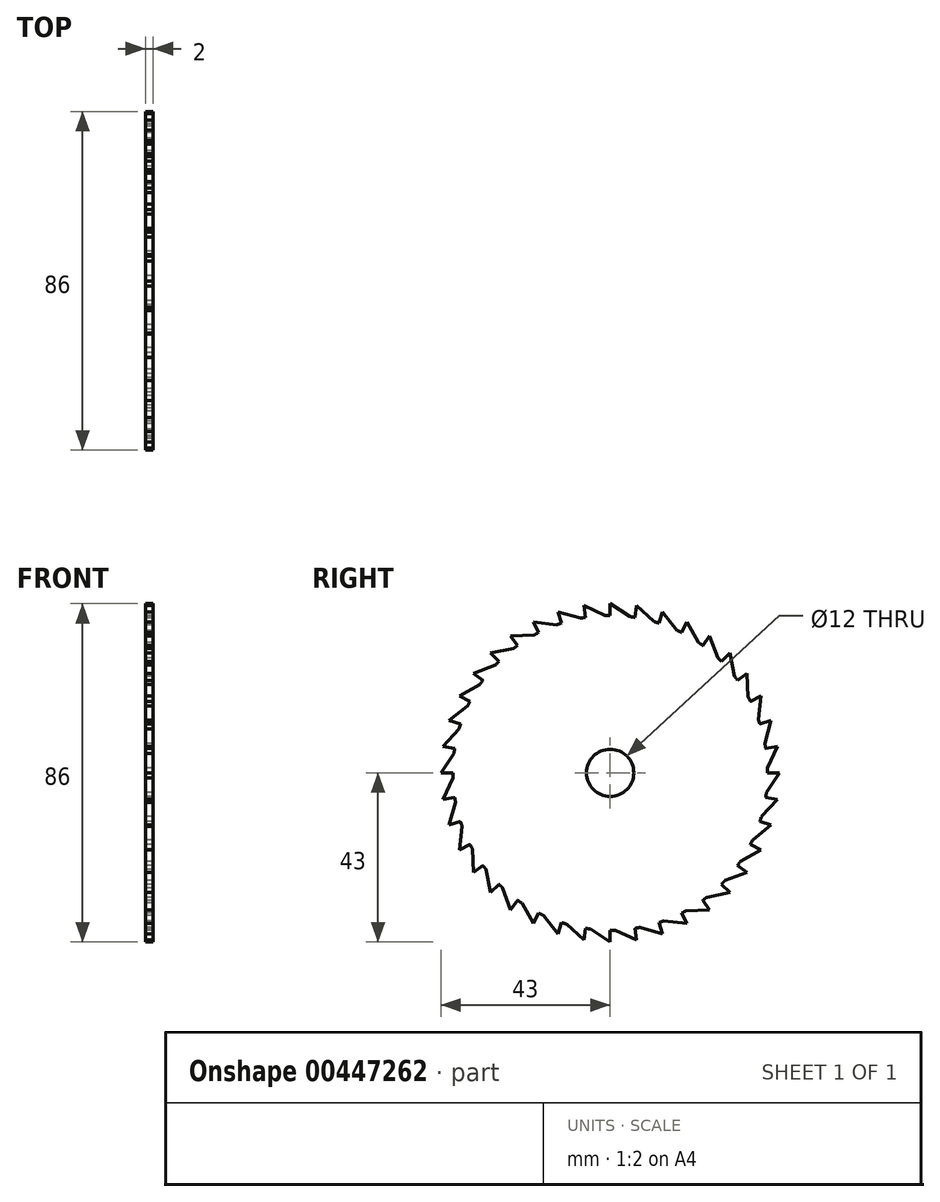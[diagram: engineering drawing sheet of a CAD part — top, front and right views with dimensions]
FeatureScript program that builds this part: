
annotation { "Feature Type Name" : "Feature", "Feature Type Description" : "" }
export const myFeature = defineFeature(function(context is Context, id is Id, definition is map)
    precondition{}
    {
        {
            var Q0;
            Q0=qCreatedBy(makeId("Right.planeOp"),FACE);
            var sketch = newSketch(context, id + "F0", { "sketchPlane" : qUnion([Q0])});
            skCircle(sketch, "E0", {"center": v(0, 0) * mm, "radius": 40 * mm});
            skLineSegment(sketch, "E1", {"start": v(0, 40) * mm, "end": v(0, 43) * mm});
            skLineSegment(sketch, "E2", {"start": v(0, 43) * mm, "end": v(5, 39.69) * mm});
            skLineSegment(sketch, "E3.1.0", {"start": v(-6.26, 39.5) * mm, "end": v(-6.73, 42.47) * mm});
            skLineSegment(sketch, "E3.1.1", {"start": v(-6.73, 42.47) * mm, "end": v(-1.28, 39.98) * mm});
            skLineSegment(sketch, "E3.2.0", {"start": v(-12.36, 38.04) * mm, "end": v(-13.29, 40.9) * mm});
            skLineSegment(sketch, "E3.2.1", {"start": v(-13.29, 40.9) * mm, "end": v(-7.52, 39.29) * mm});
            skLineSegment(sketch, "E3.3.0", {"start": v(-18.16, 35.64) * mm, "end": v(-19.52, 38.31) * mm});
            skLineSegment(sketch, "E3.3.1", {"start": v(-19.52, 38.31) * mm, "end": v(-13.57, 37.63) * mm});
            skLineSegment(sketch, "E3.4.0", {"start": v(-23.51, 32.36) * mm, "end": v(-25.27, 34.79) * mm});
            skLineSegment(sketch, "E3.4.1", {"start": v(-25.27, 34.79) * mm, "end": v(-19.3, 35.04) * mm});
            skLineSegment(sketch, "E3.5.0", {"start": v(-28.28, 28.28) * mm, "end": v(-30.4, 30.4) * mm});
            skLineSegment(sketch, "E3.5.1", {"start": v(-30.4, 30.4) * mm, "end": v(-24.53, 31.6) * mm});
            skLineSegment(sketch, "E3.6.0", {"start": v(-32.36, 23.51) * mm, "end": v(-34.79, 25.27) * mm});
            skLineSegment(sketch, "E3.6.1", {"start": v(-34.79, 25.27) * mm, "end": v(-29.17, 27.36) * mm});
            skLineSegment(sketch, "E3.7.0", {"start": v(-35.64, 18.16) * mm, "end": v(-38.31, 19.52) * mm});
            skLineSegment(sketch, "E3.7.1", {"start": v(-38.31, 19.52) * mm, "end": v(-33.1, 22.46) * mm});
            skLineSegment(sketch, "E3.8.0", {"start": v(-38.04, 12.36) * mm, "end": v(-40.9, 13.29) * mm});
            skLineSegment(sketch, "E3.8.1", {"start": v(-40.9, 13.29) * mm, "end": v(-36.2, 17.01) * mm});
            skLineSegment(sketch, "E3.9.0", {"start": v(-39.5, 6.26) * mm, "end": v(-42.47, 6.73) * mm});
            skLineSegment(sketch, "E3.9.1", {"start": v(-42.47, 6.73) * mm, "end": v(-38.42, 11.14) * mm});
            skLineSegment(sketch, "E3.10.0", {"start": v(-40, 0) * mm, "end": v(-43, 0) * mm});
            skLineSegment(sketch, "E3.10.1", {"start": v(-43, 0) * mm, "end": v(-39.69, 5) * mm});
            skLineSegment(sketch, "E3.11.0", {"start": v(-39.5, -6.26) * mm, "end": v(-42.47, -6.73) * mm});
            skLineSegment(sketch, "E3.11.1", {"start": v(-42.47, -6.73) * mm, "end": v(-39.98, -1.28) * mm});
            skLineSegment(sketch, "E3.12.0", {"start": v(-38.04, -12.36) * mm, "end": v(-40.9, -13.29) * mm});
            skLineSegment(sketch, "E3.12.1", {"start": v(-40.9, -13.29) * mm, "end": v(-39.29, -7.52) * mm});
            skLineSegment(sketch, "E3.13.0", {"start": v(-35.64, -18.16) * mm, "end": v(-38.31, -19.52) * mm});
            skLineSegment(sketch, "E3.13.1", {"start": v(-38.31, -19.52) * mm, "end": v(-37.63, -13.57) * mm});
            skLineSegment(sketch, "E3.14.0", {"start": v(-32.36, -23.51) * mm, "end": v(-34.79, -25.27) * mm});
            skLineSegment(sketch, "E3.14.1", {"start": v(-34.79, -25.27) * mm, "end": v(-35.04, -19.3) * mm});
            skLineSegment(sketch, "E3.15.0", {"start": v(-28.28, -28.28) * mm, "end": v(-30.4, -30.4) * mm});
            skLineSegment(sketch, "E3.15.1", {"start": v(-30.4, -30.4) * mm, "end": v(-31.6, -24.53) * mm});
            skLineSegment(sketch, "E3.16.0", {"start": v(-23.51, -32.36) * mm, "end": v(-25.27, -34.79) * mm});
            skLineSegment(sketch, "E3.16.1", {"start": v(-25.27, -34.79) * mm, "end": v(-27.36, -29.17) * mm});
            skLineSegment(sketch, "E3.17.0", {"start": v(-18.16, -35.64) * mm, "end": v(-19.52, -38.31) * mm});
            skLineSegment(sketch, "E3.17.1", {"start": v(-19.52, -38.31) * mm, "end": v(-22.46, -33.1) * mm});
            skLineSegment(sketch, "E3.18.0", {"start": v(-12.36, -38.04) * mm, "end": v(-13.29, -40.9) * mm});
            skLineSegment(sketch, "E3.18.1", {"start": v(-13.29, -40.9) * mm, "end": v(-17.01, -36.2) * mm});
            skLineSegment(sketch, "E3.19.0", {"start": v(-6.26, -39.5) * mm, "end": v(-6.73, -42.47) * mm});
            skLineSegment(sketch, "E3.19.1", {"start": v(-6.73, -42.47) * mm, "end": v(-11.14, -38.42) * mm});
            skLineSegment(sketch, "E3.20.0", {"start": v(0, -40) * mm, "end": v(0, -43) * mm});
            skLineSegment(sketch, "E3.20.1", {"start": v(0, -43) * mm, "end": v(-5, -39.69) * mm});
            skLineSegment(sketch, "E3.21.0", {"start": v(6.26, -39.5) * mm, "end": v(6.73, -42.47) * mm});
            skLineSegment(sketch, "E3.21.1", {"start": v(6.73, -42.47) * mm, "end": v(1.28, -39.98) * mm});
            skLineSegment(sketch, "E3.22.0", {"start": v(12.36, -38.04) * mm, "end": v(13.29, -40.9) * mm});
            skLineSegment(sketch, "E3.22.1", {"start": v(13.29, -40.9) * mm, "end": v(7.52, -39.29) * mm});
            skLineSegment(sketch, "E3.23.0", {"start": v(18.16, -35.64) * mm, "end": v(19.52, -38.31) * mm});
            skLineSegment(sketch, "E3.23.1", {"start": v(19.52, -38.31) * mm, "end": v(13.57, -37.63) * mm});
            skLineSegment(sketch, "E3.24.0", {"start": v(23.51, -32.36) * mm, "end": v(25.27, -34.79) * mm});
            skLineSegment(sketch, "E3.24.1", {"start": v(25.27, -34.79) * mm, "end": v(19.3, -35.04) * mm});
            skLineSegment(sketch, "E3.25.0", {"start": v(28.28, -28.28) * mm, "end": v(30.4, -30.4) * mm});
            skLineSegment(sketch, "E3.25.1", {"start": v(30.4, -30.4) * mm, "end": v(24.53, -31.6) * mm});
            skLineSegment(sketch, "E3.26.0", {"start": v(32.36, -23.51) * mm, "end": v(34.79, -25.27) * mm});
            skLineSegment(sketch, "E3.26.1", {"start": v(34.79, -25.27) * mm, "end": v(29.17, -27.36) * mm});
            skLineSegment(sketch, "E3.27.0", {"start": v(35.64, -18.16) * mm, "end": v(38.31, -19.52) * mm});
            skLineSegment(sketch, "E3.27.1", {"start": v(38.31, -19.52) * mm, "end": v(33.1, -22.46) * mm});
            skLineSegment(sketch, "E3.28.0", {"start": v(38.04, -12.36) * mm, "end": v(40.9, -13.29) * mm});
            skLineSegment(sketch, "E3.28.1", {"start": v(40.9, -13.29) * mm, "end": v(36.2, -17.01) * mm});
            skLineSegment(sketch, "E3.29.0", {"start": v(39.5, -6.26) * mm, "end": v(42.47, -6.73) * mm});
            skLineSegment(sketch, "E3.29.1", {"start": v(42.47, -6.73) * mm, "end": v(38.42, -11.14) * mm});
            skLineSegment(sketch, "E3.30.0", {"start": v(40, 0) * mm, "end": v(43, 0) * mm});
            skLineSegment(sketch, "E3.30.1", {"start": v(43, 0) * mm, "end": v(39.69, -5) * mm});
            skLineSegment(sketch, "E3.31.0", {"start": v(39.5, 6.26) * mm, "end": v(42.47, 6.73) * mm});
            skLineSegment(sketch, "E3.31.1", {"start": v(42.47, 6.73) * mm, "end": v(39.98, 1.28) * mm});
            skLineSegment(sketch, "E3.32.0", {"start": v(38.04, 12.36) * mm, "end": v(40.9, 13.29) * mm});
            skLineSegment(sketch, "E3.32.1", {"start": v(40.9, 13.29) * mm, "end": v(39.29, 7.52) * mm});
            skLineSegment(sketch, "E3.33.0", {"start": v(35.64, 18.16) * mm, "end": v(38.31, 19.52) * mm});
            skLineSegment(sketch, "E3.33.1", {"start": v(38.31, 19.52) * mm, "end": v(37.63, 13.57) * mm});
            skLineSegment(sketch, "E3.34.0", {"start": v(32.36, 23.51) * mm, "end": v(34.79, 25.27) * mm});
            skLineSegment(sketch, "E3.34.1", {"start": v(34.79, 25.27) * mm, "end": v(35.04, 19.3) * mm});
            skLineSegment(sketch, "E3.35.0", {"start": v(28.28, 28.28) * mm, "end": v(30.4, 30.4) * mm});
            skLineSegment(sketch, "E3.35.1", {"start": v(30.4, 30.4) * mm, "end": v(31.6, 24.53) * mm});
            skLineSegment(sketch, "E3.36.0", {"start": v(23.51, 32.36) * mm, "end": v(25.27, 34.79) * mm});
            skLineSegment(sketch, "E3.36.1", {"start": v(25.27, 34.79) * mm, "end": v(27.36, 29.17) * mm});
            skLineSegment(sketch, "E3.37.0", {"start": v(18.16, 35.64) * mm, "end": v(19.52, 38.31) * mm});
            skLineSegment(sketch, "E3.37.1", {"start": v(19.52, 38.31) * mm, "end": v(22.46, 33.1) * mm});
            skLineSegment(sketch, "E3.38.0", {"start": v(12.36, 38.04) * mm, "end": v(13.29, 40.9) * mm});
            skLineSegment(sketch, "E3.38.1", {"start": v(13.29, 40.9) * mm, "end": v(17.01, 36.2) * mm});
            skLineSegment(sketch, "E3.39.0", {"start": v(6.26, 39.5) * mm, "end": v(6.73, 42.47) * mm});
            skLineSegment(sketch, "E3.39.1", {"start": v(6.73, 42.47) * mm, "end": v(11.14, 38.42) * mm});
            skCircle(sketch, "E4", {"center": v(0, 0) * mm, "radius": 6 * mm});
            skSolve(sketch);
        }
        {
            var Q0;
            {var subQ0=sQuery(id+"F0.wireOp",EDGE,"E0");var subQ33=makeQuery(id+"F0.imprint","INTERSECT",VERTEX,{"derivedFrom":[subQ0,sQuery(id+"F0.wireOp",EDGE,"E3.30.0")]});Q0=makeQuery(id+"F0.imprint","IMPRINT",FACE,{"disambiguationData":[TD([[makeQuery(id+"F0.imprint","IMPRINT",EDGE,{"disambiguationData":[TD([[subQ33,-1.0]])],"derivedFrom":subQ0}),1.0]])]});}
            var Q1;
            {var subQ0=sQuery(id+"F0.wireOp",EDGE,"E3.17.0");Q1=makeQuery(id+"F0.imprint","IMPRINT",FACE,{"disambiguationData":[TD([[makeQuery(id+"F0.imprint","IMPRINT",EDGE,{"derivedFrom":subQ0}),-1.0]])]});}
            var Q2;
            {var subQ0=sQuery(id+"F0.wireOp",EDGE,"E3.10.0");Q2=makeQuery(id+"F0.imprint","IMPRINT",FACE,{"disambiguationData":[TD([[makeQuery(id+"F0.imprint","IMPRINT",EDGE,{"derivedFrom":subQ0}),-1.0]])]});}
            var Q3;
            {var subQ0=sQuery(id+"F0.wireOp",EDGE,"E3.26.0");Q3=makeQuery(id+"F0.imprint","IMPRINT",FACE,{"disambiguationData":[TD([[makeQuery(id+"F0.imprint","IMPRINT",EDGE,{"derivedFrom":subQ0}),-1.0]])]});}
            var Q4;
            {var subQ0=sQuery(id+"F0.wireOp",EDGE,"E3.11.0");Q4=makeQuery(id+"F0.imprint","IMPRINT",FACE,{"disambiguationData":[TD([[makeQuery(id+"F0.imprint","IMPRINT",EDGE,{"derivedFrom":subQ0}),-1.0]])]});}
            var Q5;
            {var subQ0=sQuery(id+"F0.wireOp",EDGE,"E3.20.0");Q5=makeQuery(id+"F0.imprint","IMPRINT",FACE,{"disambiguationData":[TD([[makeQuery(id+"F0.imprint","IMPRINT",EDGE,{"derivedFrom":subQ0}),-1.0]])]});}
            var Q6;
            {var subQ0=sQuery(id+"F0.wireOp",EDGE,"E3.27.0");Q6=makeQuery(id+"F0.imprint","IMPRINT",FACE,{"disambiguationData":[TD([[makeQuery(id+"F0.imprint","IMPRINT",EDGE,{"derivedFrom":subQ0}),-1.0]])]});}
            var Q7;
            {var subQ0=sQuery(id+"F0.wireOp",EDGE,"E3.18.0");Q7=makeQuery(id+"F0.imprint","IMPRINT",FACE,{"disambiguationData":[TD([[makeQuery(id+"F0.imprint","IMPRINT",EDGE,{"derivedFrom":subQ0}),-1.0]])]});}
            var Q8;
            {var subQ0=sQuery(id+"F0.wireOp",EDGE,"E3.12.0");Q8=makeQuery(id+"F0.imprint","IMPRINT",FACE,{"disambiguationData":[TD([[makeQuery(id+"F0.imprint","IMPRINT",EDGE,{"derivedFrom":subQ0}),-1.0]])]});}
            var Q9;
            {var subQ0=sQuery(id+"F0.wireOp",EDGE,"E3.28.0");Q9=makeQuery(id+"F0.imprint","IMPRINT",FACE,{"disambiguationData":[TD([[makeQuery(id+"F0.imprint","IMPRINT",EDGE,{"derivedFrom":subQ0}),-1.0]])]});}
            var Q10;
            {var subQ0=sQuery(id+"F0.wireOp",EDGE,"E3.21.0");Q10=makeQuery(id+"F0.imprint","IMPRINT",FACE,{"disambiguationData":[TD([[makeQuery(id+"F0.imprint","IMPRINT",EDGE,{"derivedFrom":subQ0}),-1.0]])]});}
            var Q11;
            {var subQ0=sQuery(id+"F0.wireOp",EDGE,"E3.19.0");Q11=makeQuery(id+"F0.imprint","IMPRINT",FACE,{"disambiguationData":[TD([[makeQuery(id+"F0.imprint","IMPRINT",EDGE,{"derivedFrom":subQ0}),-1.0]])]});}
            var Q12;
            {var subQ0=sQuery(id+"F0.wireOp",EDGE,"E3.29.0");Q12=makeQuery(id+"F0.imprint","IMPRINT",FACE,{"disambiguationData":[TD([[makeQuery(id+"F0.imprint","IMPRINT",EDGE,{"derivedFrom":subQ0}),-1.0]])]});}
            var Q13;
            {var subQ0=sQuery(id+"F0.wireOp",EDGE,"E3.13.0");Q13=makeQuery(id+"F0.imprint","IMPRINT",FACE,{"disambiguationData":[TD([[makeQuery(id+"F0.imprint","IMPRINT",EDGE,{"derivedFrom":subQ0}),-1.0]])]});}
            var Q14;
            {var subQ0=sQuery(id+"F0.wireOp",EDGE,"E3.6.0");Q14=makeQuery(id+"F0.imprint","IMPRINT",FACE,{"disambiguationData":[TD([[makeQuery(id+"F0.imprint","IMPRINT",EDGE,{"derivedFrom":subQ0}),-1.0]])]});}
            var Q15;
            {var subQ0=sQuery(id+"F0.wireOp",EDGE,"E3.4.0");Q15=makeQuery(id+"F0.imprint","IMPRINT",FACE,{"disambiguationData":[TD([[makeQuery(id+"F0.imprint","IMPRINT",EDGE,{"derivedFrom":subQ0}),-1.0]])]});}
            var Q16;
            {var subQ0=sQuery(id+"F0.wireOp",EDGE,"E3.5.0");Q16=makeQuery(id+"F0.imprint","IMPRINT",FACE,{"disambiguationData":[TD([[makeQuery(id+"F0.imprint","IMPRINT",EDGE,{"derivedFrom":subQ0}),-1.0]])]});}
            var Q17;
            {var subQ0=sQuery(id+"F0.wireOp",EDGE,"E3.7.0");Q17=makeQuery(id+"F0.imprint","IMPRINT",FACE,{"disambiguationData":[TD([[makeQuery(id+"F0.imprint","IMPRINT",EDGE,{"derivedFrom":subQ0}),-1.0]])]});}
            var Q18;
            {var subQ0=sQuery(id+"F0.wireOp",EDGE,"E3.23.0");Q18=makeQuery(id+"F0.imprint","IMPRINT",FACE,{"disambiguationData":[TD([[makeQuery(id+"F0.imprint","IMPRINT",EDGE,{"derivedFrom":subQ0}),-1.0]])]});}
            var Q19;
            {var subQ0=sQuery(id+"F0.wireOp",EDGE,"E3.31.0");Q19=makeQuery(id+"F0.imprint","IMPRINT",FACE,{"disambiguationData":[TD([[makeQuery(id+"F0.imprint","IMPRINT",EDGE,{"derivedFrom":subQ0}),-1.0]])]});}
            var Q20;
            {var subQ0=sQuery(id+"F0.wireOp",EDGE,"E3.32.0");Q20=makeQuery(id+"F0.imprint","IMPRINT",FACE,{"disambiguationData":[TD([[makeQuery(id+"F0.imprint","IMPRINT",EDGE,{"derivedFrom":subQ0}),-1.0]])]});}
            var Q21;
            {var subQ0=sQuery(id+"F0.wireOp",EDGE,"E3.33.0");Q21=makeQuery(id+"F0.imprint","IMPRINT",FACE,{"disambiguationData":[TD([[makeQuery(id+"F0.imprint","IMPRINT",EDGE,{"derivedFrom":subQ0}),-1.0]])]});}
            var Q22;
            {var subQ0=sQuery(id+"F0.wireOp",EDGE,"E3.34.0");Q22=makeQuery(id+"F0.imprint","IMPRINT",FACE,{"disambiguationData":[TD([[makeQuery(id+"F0.imprint","IMPRINT",EDGE,{"derivedFrom":subQ0}),-1.0]])]});}
            var Q23;
            {var subQ0=sQuery(id+"F0.wireOp",EDGE,"E3.35.0");Q23=makeQuery(id+"F0.imprint","IMPRINT",FACE,{"disambiguationData":[TD([[makeQuery(id+"F0.imprint","IMPRINT",EDGE,{"derivedFrom":subQ0}),-1.0]])]});}
            var Q24;
            {var subQ0=sQuery(id+"F0.wireOp",EDGE,"E3.36.0");Q24=makeQuery(id+"F0.imprint","IMPRINT",FACE,{"disambiguationData":[TD([[makeQuery(id+"F0.imprint","IMPRINT",EDGE,{"derivedFrom":subQ0}),-1.0]])]});}
            var Q25;
            {var subQ0=sQuery(id+"F0.wireOp",EDGE,"E3.37.0");Q25=makeQuery(id+"F0.imprint","IMPRINT",FACE,{"disambiguationData":[TD([[makeQuery(id+"F0.imprint","IMPRINT",EDGE,{"derivedFrom":subQ0}),-1.0]])]});}
            var Q26;
            {var subQ0=sQuery(id+"F0.wireOp",EDGE,"E3.38.0");Q26=makeQuery(id+"F0.imprint","IMPRINT",FACE,{"disambiguationData":[TD([[makeQuery(id+"F0.imprint","IMPRINT",EDGE,{"derivedFrom":subQ0}),-1.0]])]});}
            var Q27;
            {var subQ0=sQuery(id+"F0.wireOp",EDGE,"E3.39.0");Q27=makeQuery(id+"F0.imprint","IMPRINT",FACE,{"disambiguationData":[TD([[makeQuery(id+"F0.imprint","IMPRINT",EDGE,{"derivedFrom":subQ0}),-1.0]])]});}
            var Q28;
            {var subQ0=sQuery(id+"F0.wireOp",EDGE,"E1");Q28=makeQuery(id+"F0.imprint","IMPRINT",FACE,{"disambiguationData":[TD([[makeQuery(id+"F0.imprint","IMPRINT",EDGE,{"derivedFrom":subQ0}),-1.0]])]});}
            var Q29;
            {var subQ0=sQuery(id+"F0.wireOp",EDGE,"E3.1.0");Q29=makeQuery(id+"F0.imprint","IMPRINT",FACE,{"disambiguationData":[TD([[makeQuery(id+"F0.imprint","IMPRINT",EDGE,{"derivedFrom":subQ0}),-1.0]])]});}
            var Q30;
            {var subQ0=sQuery(id+"F0.wireOp",EDGE,"E3.2.0");Q30=makeQuery(id+"F0.imprint","IMPRINT",FACE,{"disambiguationData":[TD([[makeQuery(id+"F0.imprint","IMPRINT",EDGE,{"derivedFrom":subQ0}),-1.0]])]});}
            var Q31;
            {var subQ0=sQuery(id+"F0.wireOp",EDGE,"E3.3.0");Q31=makeQuery(id+"F0.imprint","IMPRINT",FACE,{"disambiguationData":[TD([[makeQuery(id+"F0.imprint","IMPRINT",EDGE,{"derivedFrom":subQ0}),-1.0]])]});}
            var Q32;
            {var subQ0=sQuery(id+"F0.wireOp",EDGE,"E3.30.0");Q32=makeQuery(id+"F0.imprint","IMPRINT",FACE,{"disambiguationData":[TD([[makeQuery(id+"F0.imprint","IMPRINT",EDGE,{"derivedFrom":subQ0}),-1.0]])]});}
            var Q33;
            {var subQ0=sQuery(id+"F0.wireOp",EDGE,"E3.14.0");Q33=makeQuery(id+"F0.imprint","IMPRINT",FACE,{"disambiguationData":[TD([[makeQuery(id+"F0.imprint","IMPRINT",EDGE,{"derivedFrom":subQ0}),-1.0]])]});}
            var Q34;
            {var subQ0=sQuery(id+"F0.wireOp",EDGE,"E3.8.0");Q34=makeQuery(id+"F0.imprint","IMPRINT",FACE,{"disambiguationData":[TD([[makeQuery(id+"F0.imprint","IMPRINT",EDGE,{"derivedFrom":subQ0}),-1.0]])]});}
            var Q35;
            {var subQ0=sQuery(id+"F0.wireOp",EDGE,"E3.24.0");Q35=makeQuery(id+"F0.imprint","IMPRINT",FACE,{"disambiguationData":[TD([[makeQuery(id+"F0.imprint","IMPRINT",EDGE,{"derivedFrom":subQ0}),-1.0]])]});}
            var Q36;
            {var subQ0=sQuery(id+"F0.wireOp",EDGE,"E3.15.0");Q36=makeQuery(id+"F0.imprint","IMPRINT",FACE,{"disambiguationData":[TD([[makeQuery(id+"F0.imprint","IMPRINT",EDGE,{"derivedFrom":subQ0}),-1.0]])]});}
            var Q37;
            {var subQ0=sQuery(id+"F0.wireOp",EDGE,"E3.9.0");Q37=makeQuery(id+"F0.imprint","IMPRINT",FACE,{"disambiguationData":[TD([[makeQuery(id+"F0.imprint","IMPRINT",EDGE,{"derivedFrom":subQ0}),-1.0]])]});}
            var Q38;
            {var subQ0=sQuery(id+"F0.wireOp",EDGE,"E3.25.0");Q38=makeQuery(id+"F0.imprint","IMPRINT",FACE,{"disambiguationData":[TD([[makeQuery(id+"F0.imprint","IMPRINT",EDGE,{"derivedFrom":subQ0}),-1.0]])]});}
            var Q39;
            {var subQ0=sQuery(id+"F0.wireOp",EDGE,"E3.22.0");Q39=makeQuery(id+"F0.imprint","IMPRINT",FACE,{"disambiguationData":[TD([[makeQuery(id+"F0.imprint","IMPRINT",EDGE,{"derivedFrom":subQ0}),-1.0]])]});}
            var Q40;
            {var subQ0=sQuery(id+"F0.wireOp",EDGE,"E3.16.0");Q40=makeQuery(id+"F0.imprint","IMPRINT",FACE,{"disambiguationData":[TD([[makeQuery(id+"F0.imprint","IMPRINT",EDGE,{"derivedFrom":subQ0}),-1.0]])]});}
            extrude(context, id + "F1", {"entities" : qUnion([Q0, Q1, Q2, Q3, Q4, Q5, Q6, Q7, Q8, Q9, Q10, Q11, Q12, Q13, Q14, Q15, Q16, Q17, Q18, Q19, Q20, Q21, Q22, Q23, Q24, Q25, Q26, Q27, Q28, Q29, Q30, Q31, Q32, Q33, Q34, Q35, Q36, Q37, Q38, Q39, Q40]), "depth" : 2 * mm});
        }
    });
